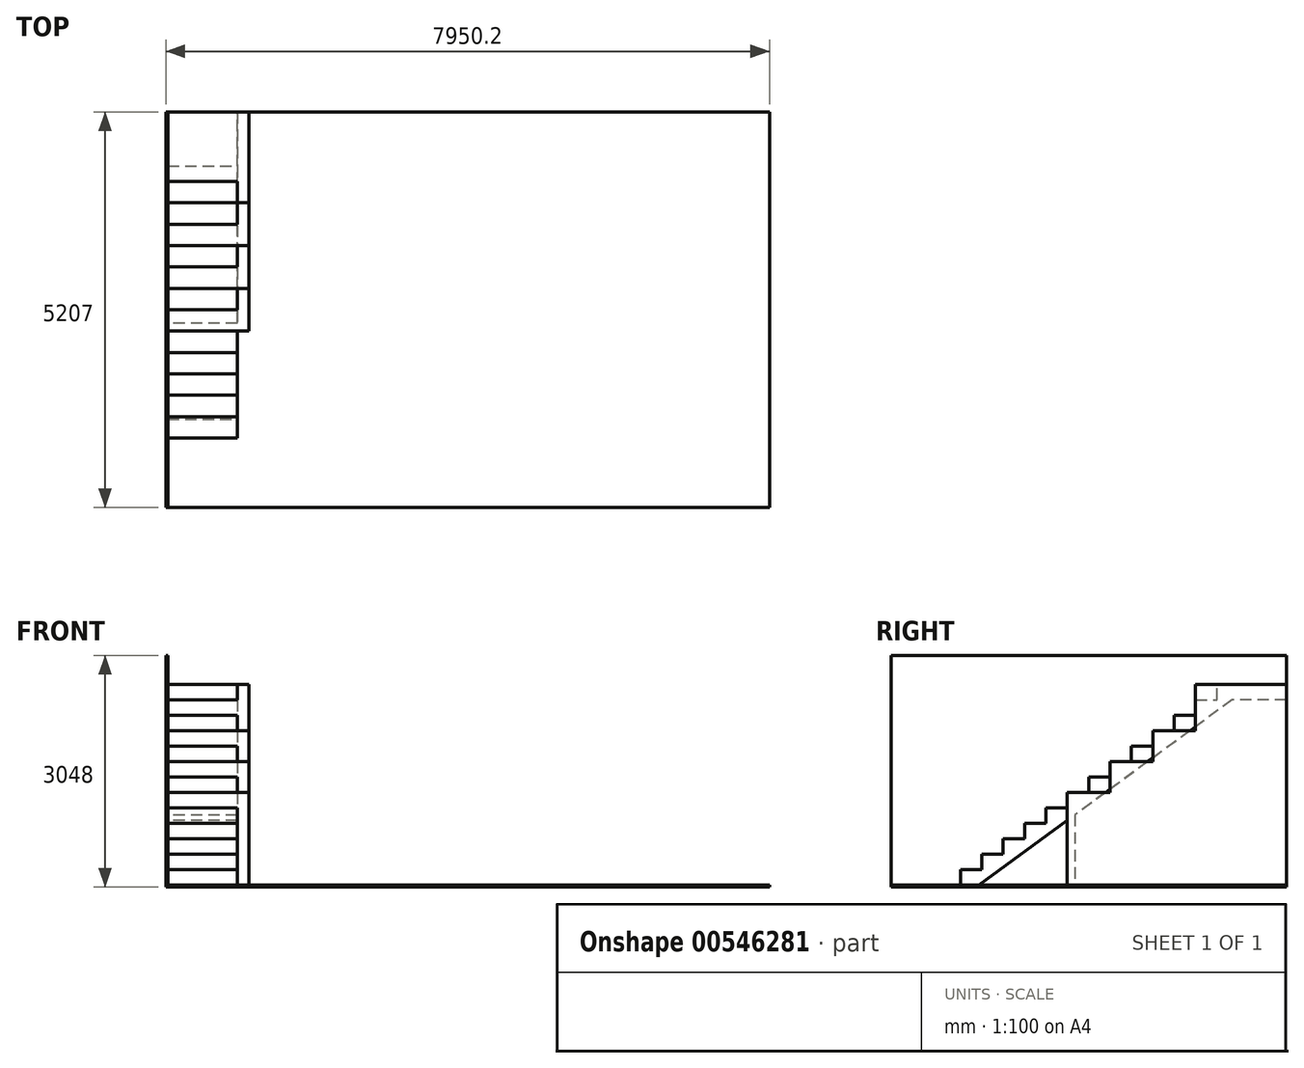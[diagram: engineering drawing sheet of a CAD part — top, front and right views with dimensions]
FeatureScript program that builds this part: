
annotation { "Feature Type Name" : "Feature", "Feature Type Description" : "" }
export const myFeature = defineFeature(function(context is Context, id is Id, definition is map)
    precondition{}
    {
        {
            var Q0;
            Q0=qCreatedBy(makeId("Top.planeOp"),FACE);
            var sketch = newSketch(context, id + "F0", { "sketchPlane" : qUnion([Q0])});
            skLineSegment(sketch, "E0.bottom", {"start": v(-3962.4, -2603.5) * mm, "end": v(-3962.4, 2603.5) * mm});
            skLineSegment(sketch, "E0.top", {"start": v(3962.4, -2603.5) * mm, "end": v(3962.4, 2603.5) * mm});
            skLineSegment(sketch, "E0.left", {"start": v(-3962.4, -2603.5) * mm, "end": v(3962.4, -2603.5) * mm});
            skLineSegment(sketch, "E0.right", {"start": v(-3962.4, 2603.5) * mm, "end": v(3962.4, 2603.5) * mm});
            skPoint(sketch, "E0.middle", {"position": v(0, 0) * mm});
            skSolve(sketch);
        }
        {
            var Q0;
            Q0 = qSketchRegion(id + "F0", true);
            extrude(context, id + "F1", {"entities" : qUnion([Q0]), "depth" : 25.4 * mm, "offsetDistance" : 25.4 * mm});
        }
        {
            var Q0;
            Q0=makeQuery(id+"F1.opExtrude","SWEPT_FACE",FACE,{"disambiguationData":[OSD([sQuery(id+"F0.wireOp",EDGE,"E0.bottom")])]});
            var sketch = newSketch(context, id + "F2", { "sketchPlane" : qUnion([Q0])});
            skLineSegment(sketch, "E1.bottom", {"start": v(2603.5, 0) * mm, "end": v(-2603.5, 0) * mm});
            skLineSegment(sketch, "E1.top", {"start": v(2603.5, 3048) * mm, "end": v(-2603.5, 3048) * mm});
            skLineSegment(sketch, "E1.left", {"start": v(-2603.5, 0) * mm, "end": v(-2603.5, 3048) * mm});
            skLineSegment(sketch, "E1.right", {"start": v(2603.5, 0) * mm, "end": v(2603.5, 3048) * mm});
            skSolve(sketch);
        }
        {
            var Q0;
            Q0 = qSketchRegion(id + "F2", true);
            extrude(context, id + "F3", {"entities" : qUnion([Q0]), "operationType" : NewBodyOperationType.ADD, "depth" : 25.4 * mm, "offsetDistance" : 25.4 * mm});
        }
        {
            var Q0;
            Q0=makeQuery(id+"F3.opExtrude","CAP_FACE",FACE,{"disambiguationData":[OSD([sQuery(id+"F2.wireOp",EDGE,"E1.bottom"),sQuery(id+"F2.wireOp",EDGE,"E1.top"),sQuery(id+"F2.wireOp",EDGE,"E1.left"),sQuery(id+"F2.wireOp",EDGE,"E1.right")])],"isStart":true});
            var sketch = newSketch(context, id + "F4", { "sketchPlane" : qUnion([Q0])});
            skLineSegment(sketch, "E2", {"start": v(-1689.1, 25.4) * mm, "end": v(-1689.1, 228.6) * mm});
            skLineSegment(sketch, "E3", {"start": v(-1689.1, 228.6) * mm, "end": v(-1407.58, 228.6) * mm});
            skLineSegment(sketch, "E4", {"start": v(-1407.58, 228.6) * mm, "end": v(-1407.58, 431.8) * mm});
            skLineSegment(sketch, "E5", {"start": v(-1407.58, 431.8) * mm, "end": v(-1126.07, 431.8) * mm});
            skLineSegment(sketch, "E6", {"start": v(-1126.07, 431.8) * mm, "end": v(-1126.07, 635) * mm});
            skLineSegment(sketch, "E7", {"start": v(-1126.07, 635) * mm, "end": v(-844.55, 635) * mm});
            skLineSegment(sketch, "E8", {"start": v(-844.55, 635) * mm, "end": v(-844.55, 838.2) * mm});
            skLineSegment(sketch, "E9", {"start": v(-844.55, 838.2) * mm, "end": v(-563.03, 838.2) * mm});
            skLineSegment(sketch, "E10", {"start": v(-563.03, 838.2) * mm, "end": v(-563.03, 1041.4) * mm});
            skLineSegment(sketch, "E11", {"start": v(-563.03, 1041.4) * mm, "end": v(-281.52, 1041.4) * mm});
            skLineSegment(sketch, "E12", {"start": v(-281.52, 1041.4) * mm, "end": v(-281.52, 1244.6) * mm});
            skLineSegment(sketch, "E13", {"start": v(-281.52, 1244.6) * mm, "end": v(0, 1244.6) * mm});
            skLineSegment(sketch, "E14", {"start": v(0, 1244.6) * mm, "end": v(0, 1447.8) * mm});
            skLineSegment(sketch, "E15", {"start": v(281.52, 1651) * mm, "end": v(563.03, 1651) * mm});
            skLineSegment(sketch, "E16", {"start": v(563.03, 1651) * mm, "end": v(563.03, 1854.2) * mm});
            skLineSegment(sketch, "E17", {"start": v(563.03, 1854.2) * mm, "end": v(844.55, 1854.2) * mm});
            skLineSegment(sketch, "E18", {"start": v(844.55, 1854.2) * mm, "end": v(844.55, 2057.4) * mm});
            skLineSegment(sketch, "E19", {"start": v(844.55, 2057.4) * mm, "end": v(1126.07, 2057.4) * mm});
            skLineSegment(sketch, "E20", {"start": v(1126.07, 2057.4) * mm, "end": v(1126.07, 2260.6) * mm});
            skLineSegment(sketch, "E21", {"start": v(1126.07, 2260.6) * mm, "end": v(1407.58, 2260.6) * mm});
            skLineSegment(sketch, "E22", {"start": v(1407.58, 2260.6) * mm, "end": v(1407.58, 2463.8) * mm});
            skLineSegment(sketch, "E23", {"start": v(1407.58, 2463.8) * mm, "end": v(1689.1, 2463.8) * mm});
            skLineSegment(sketch, "E24", {"start": v(1689.1, 2463.8) * mm, "end": v(1689.1, 2667) * mm});
            skLineSegment(sketch, "E25", {"start": v(1689.1, 2667) * mm, "end": v(2603.5, 2667) * mm});
            skLineSegment(sketch, "E26", {"start": v(281.52, 1651) * mm, "end": v(281.52, 1447.8) * mm});
            skLineSegment(sketch, "E27", {"start": v(-2603.5, 25.4) * mm, "end": v(-1689.1, 25.4) * mm, "construction": true});
            skLineSegment(sketch, "E28", {"start": v(0, 1447.8) * mm, "end": v(281.52, 1447.8) * mm});
            skLineSegment(sketch, "E29", {"start": v(2603.5, 2667) * mm, "end": v(2603.5, 25.4) * mm});
            skLineSegment(sketch, "E30", {"start": v(2603.5, 25.4) * mm, "end": v(-1689.1, 25.4) * mm});
            skSolve(sketch);
        }
        {
            var Q0;
            Q0 = qSketchRegion(id + "F4", true);
            extrude(context, id + "F5", {"entities" : qUnion([Q0]), "operationType" : NewBodyOperationType.ADD, "depth" : 914.4 * mm, "offsetDistance" : 25.4 * mm});
        }
        {
            var Q0;
            Q0=makeQuery(id+"F5.opExtrude","CAP_FACE",FACE,{"disambiguationData":[OSD([sQuery(id+"F4.wireOp",EDGE,"E2"),sQuery(id+"F4.wireOp",EDGE,"E3"),sQuery(id+"F4.wireOp",EDGE,"E4"),sQuery(id+"F4.wireOp",EDGE,"E5"),sQuery(id+"F4.wireOp",EDGE,"E6"),sQuery(id+"F4.wireOp",EDGE,"E7"),sQuery(id+"F4.wireOp",EDGE,"E8"),sQuery(id+"F4.wireOp",EDGE,"E9"),sQuery(id+"F4.wireOp",EDGE,"E10"),sQuery(id+"F4.wireOp",EDGE,"E11"),sQuery(id+"F4.wireOp",EDGE,"E12"),sQuery(id+"F4.wireOp",EDGE,"E13"),sQuery(id+"F4.wireOp",EDGE,"E14"),sQuery(id+"F4.wireOp",EDGE,"E15"),sQuery(id+"F4.wireOp",EDGE,"E16"),sQuery(id+"F4.wireOp",EDGE,"E17"),sQuery(id+"F4.wireOp",EDGE,"E18"),sQuery(id+"F4.wireOp",EDGE,"E19"),sQuery(id+"F4.wireOp",EDGE,"E20"),sQuery(id+"F4.wireOp",EDGE,"E21"),sQuery(id+"F4.wireOp",EDGE,"E22"),sQuery(id+"F4.wireOp",EDGE,"E23"),sQuery(id+"F4.wireOp",EDGE,"E24"),sQuery(id+"F4.wireOp",EDGE,"E25"),sQuery(id+"F4.wireOp",EDGE,"E26"),sQuery(id+"F4.wireOp",EDGE,"E28"),sQuery(id+"F4.wireOp",EDGE,"E29"),sQuery(id+"F4.wireOp",EDGE,"E30")])],"isStart":false});
            var sketch = newSketch(context, id + "F6", { "sketchPlane" : qUnion([Q0])});
            skLineSegment(sketch, "E31", {"start": v(2603.5, 2463.8) * mm, "end": v(1891.87, 2463.8) * mm});
            skLineSegment(sketch, "E32", {"start": v(1891.87, 2463.8) * mm, "end": v(-1444.63, 25.4) * mm});
            skLineSegment(sketch, "E33", {"start": v(-1444.63, 25.4) * mm, "end": v(2603.5, 25.4) * mm});
            skLineSegment(sketch, "E34", {"start": v(2603.5, 25.4) * mm, "end": v(2603.5, 2463.8) * mm});
            skLineSegment(sketch, "E35", {"start": v(-1407.58, 406.4) * mm, "end": v(-1126.07, 406.4) * mm, "construction": true});
            skLineSegment(sketch, "E36", {"start": v(1407.58, 2463.8) * mm, "end": v(1576.19, 2233.1) * mm, "construction": true});
            skSolve(sketch);
        }
        {
            var Q0;
            Q0=makeQuery(id+"F6.imprint","IMPRINT",FACE,{"disambiguationData":[TD([[makeQuery(id+"F6.imprint","IMPRINT",EDGE,{"derivedFrom":sQuery(id+"F6.wireOp",EDGE,"E31")}),1.0]])]});
            var Q1;
            Q1=makeQuery(id+"F3.opExtrude","CAP_FACE",FACE,{"disambiguationData":[OSD([sQuery(id+"F2.wireOp",EDGE,"E1.bottom"),sQuery(id+"F2.wireOp",EDGE,"E1.top"),sQuery(id+"F2.wireOp",EDGE,"E1.left"),sQuery(id+"F2.wireOp",EDGE,"E1.right")])],"isStart":true});
            extrude(context, id + "F7", {"entities" : qUnion([Q0]), "operationType" : NewBodyOperationType.REMOVE, "endBound" : BoundingType.UP_TO_SURFACE, "oppositeDirection" : true, "depth" : 25.4 * mm, "endBoundEntityFace" : qUnion([Q1]), "offsetDistance" : 25.4 * mm});
        }
        {
            var Q0;
            Q0=makeQuery(id+"F5.opExtrude","CAP_FACE",FACE,{"disambiguationData":[OSD([sQuery(id+"F4.wireOp",EDGE,"E2"),sQuery(id+"F4.wireOp",EDGE,"E3"),sQuery(id+"F4.wireOp",EDGE,"E4"),sQuery(id+"F4.wireOp",EDGE,"E5"),sQuery(id+"F4.wireOp",EDGE,"E6"),sQuery(id+"F4.wireOp",EDGE,"E7"),sQuery(id+"F4.wireOp",EDGE,"E8"),sQuery(id+"F4.wireOp",EDGE,"E9"),sQuery(id+"F4.wireOp",EDGE,"E10"),sQuery(id+"F4.wireOp",EDGE,"E11"),sQuery(id+"F4.wireOp",EDGE,"E12"),sQuery(id+"F4.wireOp",EDGE,"E13"),sQuery(id+"F4.wireOp",EDGE,"E14"),sQuery(id+"F4.wireOp",EDGE,"E15"),sQuery(id+"F4.wireOp",EDGE,"E16"),sQuery(id+"F4.wireOp",EDGE,"E17"),sQuery(id+"F4.wireOp",EDGE,"E18"),sQuery(id+"F4.wireOp",EDGE,"E19"),sQuery(id+"F4.wireOp",EDGE,"E20"),sQuery(id+"F4.wireOp",EDGE,"E21"),sQuery(id+"F4.wireOp",EDGE,"E22"),sQuery(id+"F4.wireOp",EDGE,"E23"),sQuery(id+"F4.wireOp",EDGE,"E24"),sQuery(id+"F4.wireOp",EDGE,"E25"),sQuery(id+"F4.wireOp",EDGE,"E26"),sQuery(id+"F4.wireOp",EDGE,"E28"),sQuery(id+"F4.wireOp",EDGE,"E29"),sQuery(id+"F4.wireOp",EDGE,"E30")])],"isStart":false});
            var sketch = newSketch(context, id + "F8", { "sketchPlane" : qUnion([Q0])});
            skLineSegment(sketch, "E37", {"start": v(2603.5, 2667) * mm, "end": v(1407.58, 2667) * mm});
            skLineSegment(sketch, "E38", {"start": v(1407.58, 2667) * mm, "end": v(1407.58, 2057.4) * mm});
            skLineSegment(sketch, "E39", {"start": v(1407.58, 2057.4) * mm, "end": v(844.55, 2057.4) * mm});
            skLineSegment(sketch, "E40", {"start": v(844.55, 2057.4) * mm, "end": v(844.55, 1651) * mm});
            skLineSegment(sketch, "E41", {"start": v(844.55, 1651) * mm, "end": v(281.52, 1651) * mm});
            skLineSegment(sketch, "E42", {"start": v(281.52, 1651) * mm, "end": v(281.52, 1244.6) * mm});
            skLineSegment(sketch, "E43", {"start": v(281.52, 1244.6) * mm, "end": v(-281.52, 1244.6) * mm});
            skLineSegment(sketch, "E44", {"start": v(-281.52, 1244.6) * mm, "end": v(-281.52, 25.4) * mm});
            skLineSegment(sketch, "E45", {"start": v(-281.52, 25.4) * mm, "end": v(2603.5, 25.4) * mm});
            skLineSegment(sketch, "E46", {"start": v(2603.5, 25.4) * mm, "end": v(2603.5, 2667) * mm});
            skSolve(sketch);
        }
        {
            var Q0;
            Q0 = qSketchRegion(id + "F8", true);
            extrude(context, id + "F9", {"entities" : qUnion([Q0]), "operationType" : NewBodyOperationType.ADD, "depth" : 152.4 * mm, "offsetDistance" : 25.4 * mm});
        }
        {
            var Q0;
            Q0=makeQuery(id+"F7.boolean.opBoolean","MERGE",FACE,{"derivedFrom":[makeQuery(id+"F1.opExtrude","CAP_FACE",FACE,{"disambiguationData":[OSD([sQuery(id+"F0.wireOp",EDGE,"E0.bottom"),sQuery(id+"F0.wireOp",EDGE,"E0.top"),sQuery(id+"F0.wireOp",EDGE,"E0.left"),sQuery(id+"F0.wireOp",EDGE,"E0.right")])],"isStart":false}),makeQuery(id+"F7.opExtrude","SWEPT_FACE",FACE,{"disambiguationData":[OSD([sQuery(id+"F6.wireOp",EDGE,"E33")])]})]});
            var sketch = newSketch(context, id + "F10", { "sketchPlane" : qUnion([Q0])});
            skLineSegment(sketch, "E47.bottom", {"start": v(-3048, -281.52) * mm, "end": v(-3962.4, -281.52) * mm});
            skLineSegment(sketch, "E47.top", {"start": v(-3048, -179.92) * mm, "end": v(-3962.4, -179.92) * mm});
            skLineSegment(sketch, "E47.left", {"start": v(-3048, -281.52) * mm, "end": v(-3048, -179.92) * mm});
            skLineSegment(sketch, "E47.right", {"start": v(-3962.4, -281.52) * mm, "end": v(-3962.4, -179.92) * mm});
            skSolve(sketch);
        }
        {
            var Q0;
            Q0 = qSketchRegion(id + "F10", true);
            var Q1;
            Q1=makeQuery(id+"F7.boolean.opBoolean","COPY",FACE,{"derivedFrom":makeQuery(id+"F7.opExtrude","SWEPT_FACE",FACE,{"disambiguationData":[OSD([sQuery(id+"F6.wireOp",EDGE,"E32")])]})});
            extrude(context, id + "F11", {"entities" : qUnion([Q0]), "operationType" : NewBodyOperationType.ADD, "endBound" : BoundingType.UP_TO_SURFACE, "depth" : 25.4 * mm, "endBoundEntityFace" : qUnion([Q1]), "offsetDistance" : 25.4 * mm});
        }
    });
